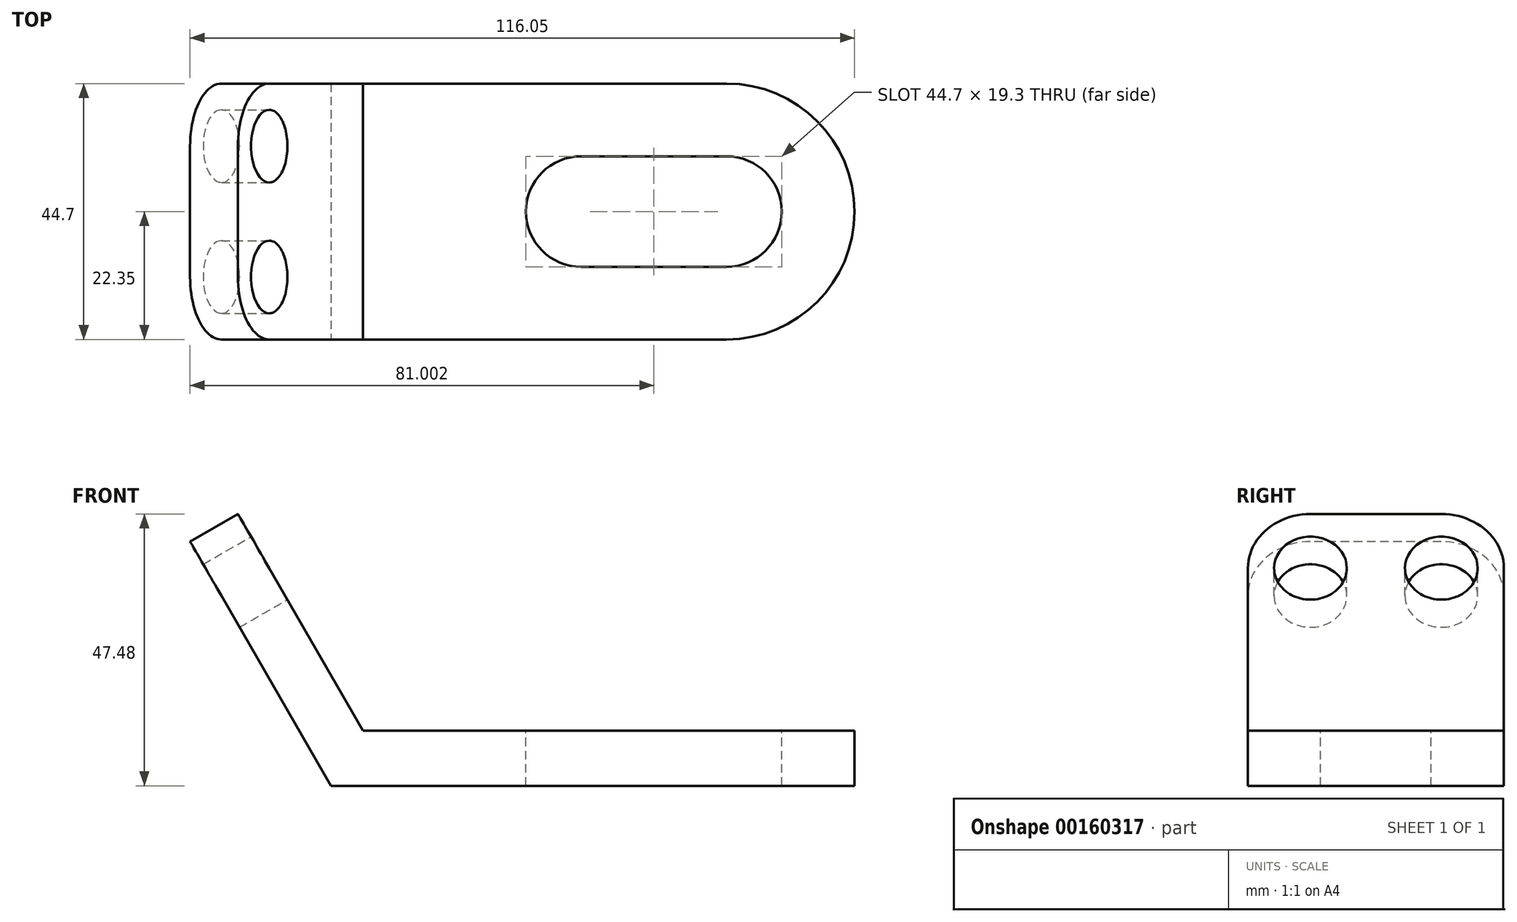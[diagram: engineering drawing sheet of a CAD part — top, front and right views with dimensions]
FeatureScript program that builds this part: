
annotation { "Feature Type Name" : "Feature", "Feature Type Description" : "" }
export const myFeature = defineFeature(function(context is Context, id is Id, definition is map)
    precondition{}
    {
        {
            var Q0;
            Q0=qCreatedBy(makeId("Top.planeOp"),FACE);
            var sketch = newSketch(context, id + "F0", { "sketchPlane" : qUnion([Q0])});
            skArc(sketch, "E0", {"start": v(0.31, -9.65) * mm, "mid": v(9.96, 0) * mm, "end": v(0.31, 9.65) * mm});
            skArc(sketch, "E1", {"start": v(-25.09, 9.65) * mm, "mid": v(-34.74, 0) * mm, "end": v(-25.09, -9.65) * mm});
            skArc(sketch, "E2", {"start": v(0.31, -22.35) * mm, "mid": v(22.66, 0) * mm, "end": v(0.31, 22.35) * mm});
            skLineSegment(sketch, "E3", {"start": v(0.31, 22.35) * mm, "end": v(-63.19, 22.35) * mm});
            skLineSegment(sketch, "E4", {"start": v(0.31, -22.35) * mm, "end": v(-63.19, -22.35) * mm});
            skLineSegment(sketch, "E5", {"start": v(-63.19, -22.35) * mm, "end": v(-63.19, 22.35) * mm});
            skLineSegment(sketch, "E6", {"start": v(-25.09, 9.65) * mm, "end": v(0.31, 9.65) * mm});
            skLineSegment(sketch, "E7", {"start": v(-25.09, -9.65) * mm, "end": v(0.31, -9.65) * mm});
            skSolve(sketch);
        }
        {
            var Q0;
            Q0=sQuery(id+"F0.wireOp",EDGE,"E5");
            cPlane(context, id + "F1", {"entities" : qUnion([Q0]), "cplaneType" : CPlaneType.LINE_ANGLE, "offset" : 25.4 * mm, "angle" : 60 * degree, "width" : 152.4 * mm, "height" : 152.4 * mm});
        }
        {
            var Q0;
            Q0=qCreatedBy(id+"F1.planeOp",FACE);
            var sketch = newSketch(context, id + "F2", { "sketchPlane" : qUnion([Q0])});
            skLineSegment(sketch, "E8.0", {"start": v(-22.35, 31.6) * mm, "end": v(22.35, 31.6) * mm});
            skLineSegment(sketch, "E9", {"start": v(-22.35, 31.6) * mm, "end": v(-22.35, 64.36) * mm});
            skLineSegment(sketch, "E10", {"start": v(22.35, 31.6) * mm, "end": v(22.35, 64.36) * mm});
            skLineSegment(sketch, "E11", {"start": v(11.43, 75.28) * mm, "end": v(-11.43, 75.28) * mm});
            skCircle(sketch, "E12", {"center": v(-11.43, 64.36) * mm, "radius": 6.35 * mm});
            skCircle(sketch, "E13", {"center": v(11.43, 64.36) * mm, "radius": 6.35 * mm});
            skCircle(sketch, "E14", {"center": v(-11.43, 64.36) * mm, "radius": 3.18 * mm});
            skCircle(sketch, "E15", {"center": v(11.43, 64.36) * mm, "radius": 3.18 * mm});
            skCircle(sketch, "E16", {"center": v(-11.43, 64.36) * mm, "radius": 1.59 * mm});
            skCircle(sketch, "E17", {"center": v(11.43, 64.36) * mm, "radius": 1.59 * mm});
            skPoint(sketch, "E18.visualSharp", {"position": v(-22.35, 75.28) * mm});
            skArc(sketch, "E18.filletArc", {"start": v(-11.43, 75.28) * mm, "mid": v(-19.15, 72.08) * mm, "end": v(-22.35, 64.36) * mm});
            skPoint(sketch, "E19.visualSharp", {"position": v(22.35, 75.28) * mm});
            skArc(sketch, "E19.filletArc", {"start": v(22.35, 64.36) * mm, "mid": v(19.15, 72.08) * mm, "end": v(11.43, 75.28) * mm});
            skSolve(sketch);
        }
        {
            var Q0;
            Q0=makeQuery(id+"F2.imprint","IMPRINT",FACE,{"disambiguationData":[TD([[makeQuery(id+"F2.imprint","IMPRINT",EDGE,{"derivedFrom":sQuery(id+"F2.wireOp",EDGE,"E8.0")}),1.0]])]});
            extrude(context, id + "F3", {"entities" : qUnion([Q0]), "oppositeDirection" : true, "depth" : 9.65 * mm});
        }
        {
            var Q0;
            Q0=makeQuery(id+"F0.imprint","IMPRINT",FACE,{"disambiguationData":[TD([[makeQuery(id+"F0.imprint","IMPRINT",EDGE,{"derivedFrom":sQuery(id+"F0.wireOp",EDGE,"E0")}),-1.0]])]});
            extrude(context, id + "F4", {"entities" : qUnion([Q0]), "oppositeDirection" : true, "depth" : 9.65 * mm});
        }
        {
            var Q0;
            Q0=makeQuery(id+"F4.opExtrude","SWEPT_FACE",FACE,{"disambiguationData":[OSD([sQuery(id+"F0.wireOp",EDGE,"E4")])]});
            var sketch = newSketch(context, id + "F5", { "sketchPlane" : qUnion([Q0])});
            skLineSegment(sketch, "E20.0", {"start": v(-71.55, -4.83) * mm, "end": v(-63.19, 0) * mm});
            skLineSegment(sketch, "E21.0", {"start": v(-63.19, -9.65) * mm, "end": v(-63.19, 0) * mm});
            skLineSegment(sketch, "E22.0", {"start": v(-71.55, -4.83) * mm, "end": v(-87.93, 23.55) * mm});
            skLineSegment(sketch, "E23", {"start": v(-71.55, -4.83) * mm, "end": v(-68.76, -9.65) * mm});
            skLineSegment(sketch, "E24", {"start": v(-68.76, -9.65) * mm, "end": v(-63.19, -9.65) * mm});
            skSolve(sketch);
        }
        {
            var Q0;
            Q0=makeQuery(id+"F5.imprint","IMPRINT",FACE,{"disambiguationData":[TD([[makeQuery(id+"F5.imprint","IMPRINT",EDGE,{"derivedFrom":sQuery(id+"F5.wireOp",EDGE,"E20.0")}),-1.0]])]});
            extrude(context, id + "F6", {"entities" : qUnion([Q0]), "operationType" : NewBodyOperationType.ADD, "oppositeDirection" : true, "depth" : 44.7 * mm});
        }
    });
